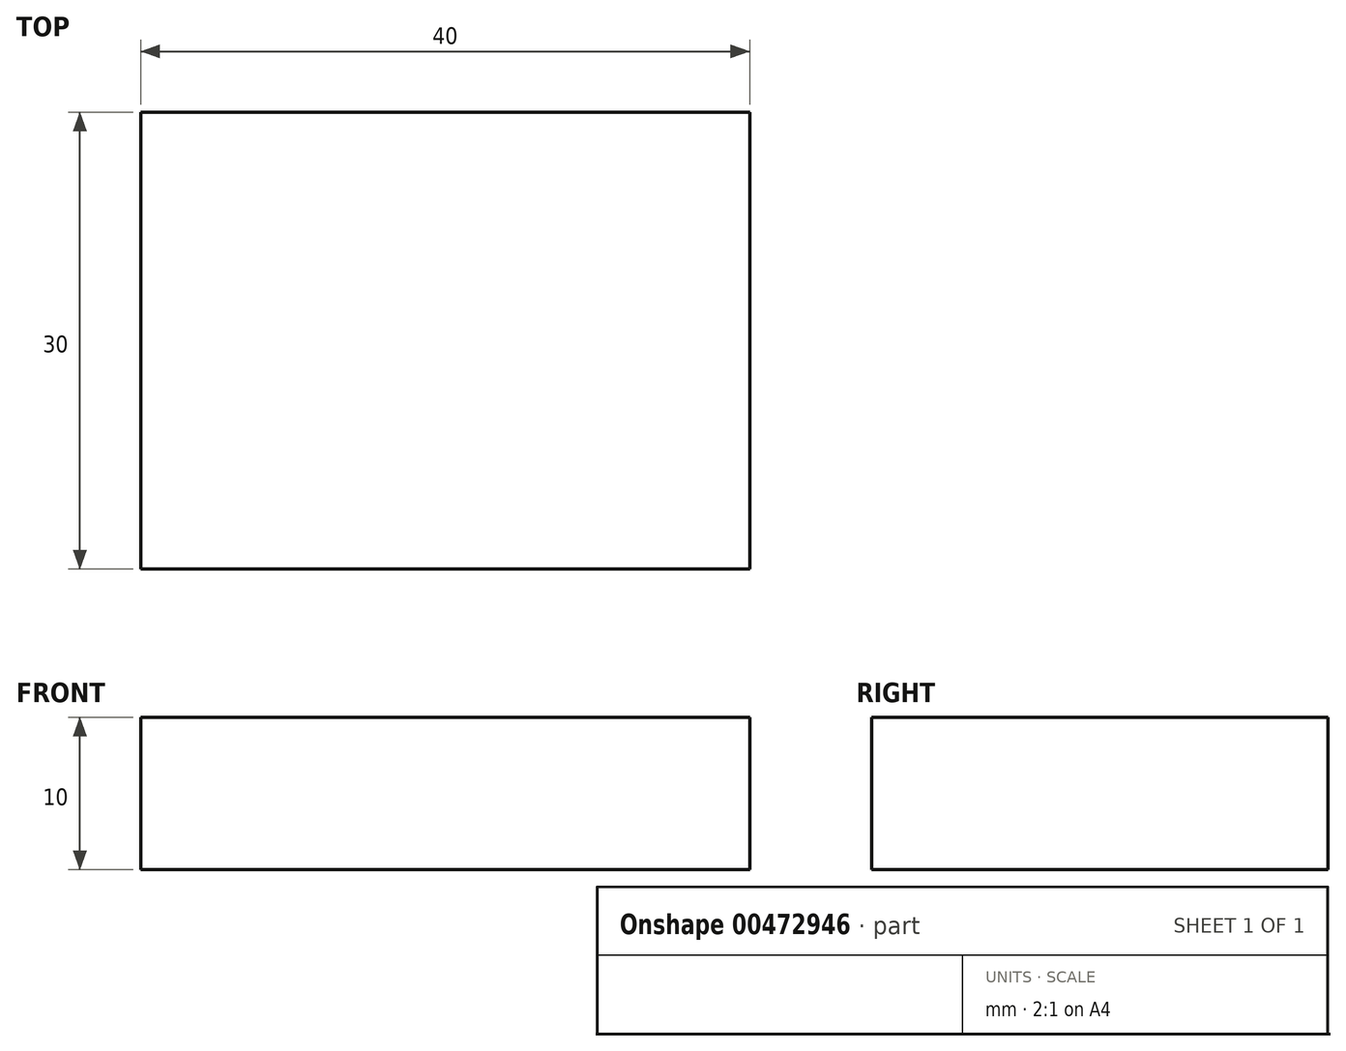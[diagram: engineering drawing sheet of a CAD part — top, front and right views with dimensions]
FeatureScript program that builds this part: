
annotation { "Feature Type Name" : "Feature", "Feature Type Description" : "" }
export const myFeature = defineFeature(function(context is Context, id is Id, definition is map)
    precondition{}
    {
        {
            var Q0;
            Q0=qCreatedBy(makeId("Top.planeOp"),FACE);
            var sketch = newSketch(context, id + "F0", { "sketchPlane" : qUnion([Q0])});
            skLineSegment(sketch, "E0.bottom", {"start": v(20, -15) * mm, "end": v(-20, -15) * mm});
            skLineSegment(sketch, "E0.top", {"start": v(20, 15) * mm, "end": v(-20, 15) * mm});
            skLineSegment(sketch, "E0.left", {"start": v(20, -15) * mm, "end": v(20, 15) * mm});
            skLineSegment(sketch, "E0.right", {"start": v(-20, -15) * mm, "end": v(-20, 15) * mm});
            skPoint(sketch, "E0.middle", {"position": v(0, 0) * mm});
            skSolve(sketch);
        }
        {
            var Q0;
            Q0 = qSketchRegion(id + "F0", true);
            extrude(context, id + "F1", {"entities" : qUnion([Q0]), "endBound" : BoundingType.SYMMETRIC, "depth" : 10 * mm});
        }
    });
